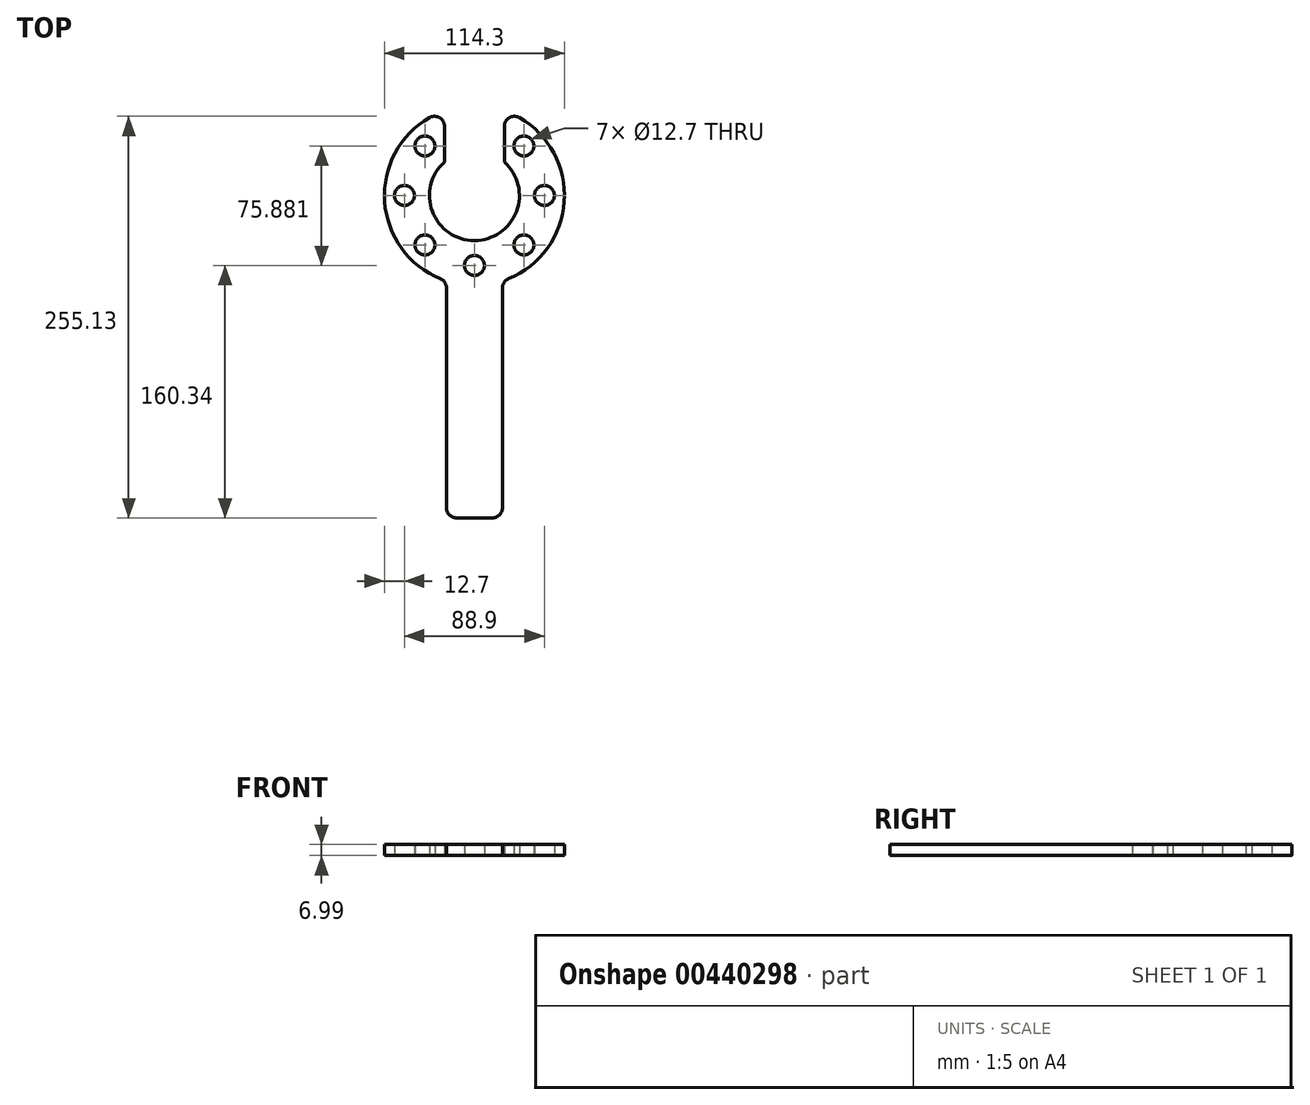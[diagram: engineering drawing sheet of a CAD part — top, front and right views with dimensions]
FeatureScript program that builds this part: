
annotation { "Feature Type Name" : "Feature", "Feature Type Description" : "" }
export const myFeature = defineFeature(function(context is Context, id is Id, definition is map)
    precondition{}
    {
        {
            var Q0;
            Q0=qCreatedBy(makeId("Top.planeOp"),FACE);
            var sketch = newSketch(context, id + "F0", { "sketchPlane" : qUnion([Q0])});
            skArc(sketch, "E0", {"start": v(-28.57, 49.5) * mm, "mid": v(-57.02, -3.82) * mm, "end": v(-21.72, -52.86) * mm});
            skArc(sketch, "E1", {"start": v(-19.05, 21.3) * mm, "mid": v(0, -28.57) * mm, "end": v(19.05, 21.3) * mm});
            skCircle(sketch, "E2", {"center": v(-44.45, 0) * mm, "radius": 6.35 * mm});
            skCircle(sketch, "E3.1.0", {"center": v(-31.43, -31.43) * mm, "radius": 6.35 * mm});
            skCircle(sketch, "E3.2.0", {"center": v(0, -44.45) * mm, "radius": 6.35 * mm});
            skCircle(sketch, "E3.3.0", {"center": v(31.43, -31.43) * mm, "radius": 6.35 * mm});
            skCircle(sketch, "E3.4.0", {"center": v(44.45, 0) * mm, "radius": 6.35 * mm});
            skCircle(sketch, "E3.5.0", {"center": v(31.43, 31.43) * mm, "radius": 6.35 * mm});
            skCircle(sketch, "E3.7.0", {"center": v(-31.43, 31.43) * mm, "radius": 6.35 * mm});
            skLineSegment(sketch, "E4", {"start": v(0, 0) * mm, "end": v(-19.05, 0) * mm, "construction": true});
            skLineSegment(sketch, "E5", {"start": v(-19.05, 21.3) * mm, "end": v(-19.05, 44) * mm});
            skLineSegment(sketch, "E6.MirrorCS", {"start": v(19.05, 21.3) * mm, "end": v(19.05, 44) * mm});
            skPoint(sketch, "E7.orphan", {"position": v(19.05, 0) * mm});
            skPoint(sketch, "E8.orphan", {"position": v(-19.05, 67.04) * mm});
            skPoint(sketch, "E9.orphan", {"position": v(19.05, 67.04) * mm});
            skPoint(sketch, "E10.visualSharp", {"position": v(-19.05, 53.88) * mm});
            skArc(sketch, "E10.filletArc", {"start": v(-19.05, 44) * mm, "mid": v(-22.22, 49.5) * mm, "end": v(-28.57, 49.5) * mm});
            skPoint(sketch, "E11.visualSharp", {"position": v(19.05, 53.88) * mm});
            skArc(sketch, "E11.filletArc", {"start": v(28.58, 49.5) * mm, "mid": v(22.23, 49.5) * mm, "end": v(19.05, 44) * mm});
            skLineSegment(sketch, "E12", {"start": v(-31.43, -31.43) * mm, "end": v(0, -44.45) * mm, "construction": true});
            skLineSegment(sketch, "E13", {"start": v(-15.72, -37.94) * mm, "end": v(-13.77, -33.25) * mm, "construction": true});
            skPoint(sketch, "E14", {"position": v(-13.77, -33.25) * mm});
            skLineSegment(sketch, "E15", {"start": v(-15.72, -37.94) * mm, "end": v(-19.36, -46.74) * mm, "construction": true});
            skPoint(sketch, "E16", {"position": v(-19.36, -46.74) * mm});
            skPoint(sketch, "E17.MirrorP", {"position": v(13.77, -33.25) * mm});
            skPoint(sketch, "E18.MirrorP", {"position": v(19.36, -46.74) * mm});
            skLineSegment(sketch, "E19.top", {"start": v(-11.43, -204.79) * mm, "end": v(11.43, -204.79) * mm});
            skLineSegment(sketch, "E19.left", {"start": v(-17.78, -58.74) * mm, "end": v(-17.78, -198.44) * mm});
            skLineSegment(sketch, "E19.right", {"start": v(17.78, -58.74) * mm, "end": v(17.78, -198.44) * mm});
            skPoint(sketch, "E19.middle", {"position": v(0, -129.55) * mm});
            skPoint(sketch, "E20.visualSharp", {"position": v(-17.78, -204.79) * mm});
            skArc(sketch, "E20.filletArc", {"start": v(-17.78, -198.44) * mm, "mid": v(-15.92, -202.93) * mm, "end": v(-11.43, -204.79) * mm});
            skPoint(sketch, "E21.visualSharp", {"position": v(17.78, -204.79) * mm});
            skArc(sketch, "E21.filletArc", {"start": v(11.43, -204.79) * mm, "mid": v(15.92, -202.93) * mm, "end": v(17.78, -198.44) * mm});
            skArc(sketch, "E22.trimOffspring", {"start": v(21.72, -52.86) * mm, "mid": v(57.02, -3.82) * mm, "end": v(28.58, 49.5) * mm});
            skPoint(sketch, "E23.visualSharp", {"position": v(17.78, -54.31) * mm});
            skArc(sketch, "E23.filletArc", {"start": v(21.72, -52.86) * mm, "mid": v(18.86, -55.2) * mm, "end": v(17.78, -58.74) * mm});
            skPoint(sketch, "E24.visualSharp", {"position": v(-17.78, -54.31) * mm});
            skArc(sketch, "E24.filletArc", {"start": v(-17.78, -58.74) * mm, "mid": v(-18.86, -55.2) * mm, "end": v(-21.72, -52.86) * mm});
            skSolve(sketch);
        }
        {
            var Q0;
            Q0 = qSketchRegion(id + "F0", true);
            extrude(context, id + "F1", {"entities" : qUnion([Q0]), "depth" : 7 * mm});
        }
    });
